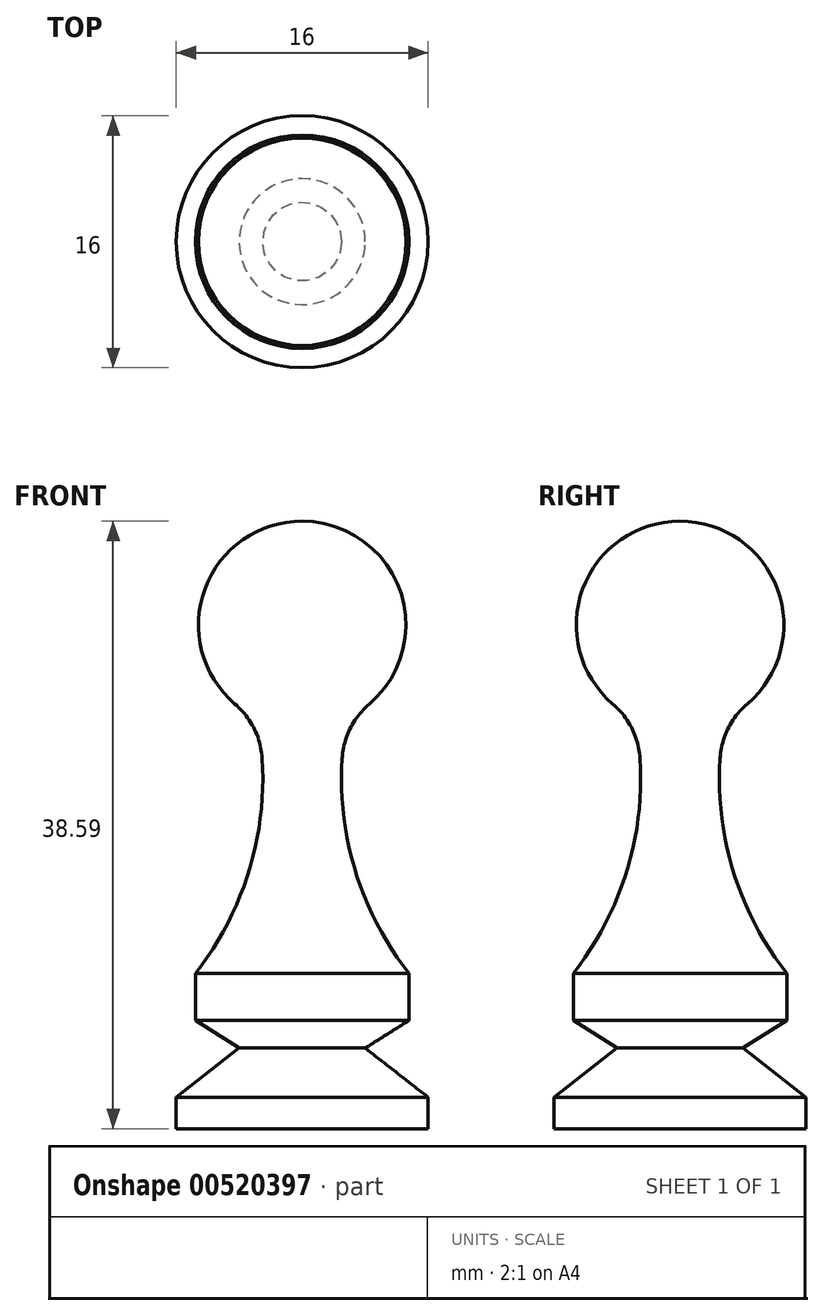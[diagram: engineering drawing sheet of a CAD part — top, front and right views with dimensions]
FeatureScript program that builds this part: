
annotation { "Feature Type Name" : "Feature", "Feature Type Description" : "" }
export const myFeature = defineFeature(function(context is Context, id is Id, definition is map)
    precondition{}
    {
        {
            var Q0;
            Q0=qCreatedBy(makeId("Front.planeOp"),FACE);
            var sketch = newSketch(context, id + "F0", { "sketchPlane" : qUnion([Q0])});
            skArc(sketch, "E0", {"start": v(0, 38.6) * mm, "mid": v(-6.42, 33.47) * mm, "end": v(-2.87, 26.07) * mm});
            skLineSegment(sketch, "E1", {"start": v(0, 0) * mm, "end": v(-8, 0) * mm});
            skLineSegment(sketch, "E2", {"start": v(-8, 0) * mm, "end": v(-8, 2) * mm});
            skLineSegment(sketch, "E3", {"start": v(-8, 2) * mm, "end": v(0, 2) * mm});
            skLineSegment(sketch, "E4", {"start": v(0, 38.6) * mm, "end": v(0, 0) * mm});
            skLineSegment(sketch, "E5", {"start": v(-2.87, 26.07) * mm, "end": v(0, 26.07) * mm});
            skPoint(sketch, "E6.start.orphan", {"position": v(0, 5.14) * mm});
            skLineSegment(sketch, "E7", {"start": v(-4, 5.12) * mm, "end": v(-8, 2) * mm});
            skLineSegment(sketch, "E8", {"start": v(-4, 5.12) * mm, "end": v(0, 5.14) * mm});
            skLineSegment(sketch, "E9", {"start": v(0, 32) * mm, "end": v(0, 0) * mm});
            skLineSegment(sketch, "E10", {"start": v(-6.78, 6.87) * mm, "end": v(0, 6.87) * mm});
            skLineSegment(sketch, "E11", {"start": v(-6.78, 6.87) * mm, "end": v(-6.78, 9.87) * mm});
            skLineSegment(sketch, "E12", {"start": v(-4, 5.12) * mm, "end": v(-6.78, 6.87) * mm});
            skArc(sketch, "E13", {"start": v(-6.78, 9.87) * mm, "mid": v(-3.06, 17.54) * mm, "end": v(-2.87, 26.07) * mm});
            skSolve(sketch);
        }
        {
            var Q0;
            Q0=makeQuery(id+"F0.imprint","IMPRINT",FACE,{"disambiguationData":[TD([[makeQuery(id+"F0.imprint","IMPRINT",EDGE,{"derivedFrom":sQuery(id+"F0.wireOp",EDGE,"E0")}),1.0]])]});
            var Q1;
            {var subQ0=sQuery(id+"F0.wireOp",EDGE,"E1");Q1=makeQuery(id+"F0.imprint","IMPRINT",FACE,{"disambiguationData":[TD([[makeQuery(id+"F0.imprint","IMPRINT",EDGE,{"derivedFrom":subQ0}),-1.0]])]});}
            var Q2;
            {var subQ0=sQuery(id+"F0.wireOp",EDGE,"E3");Q2=makeQuery(id+"F0.imprint","IMPRINT",FACE,{"disambiguationData":[TD([[makeQuery(id+"F0.imprint","IMPRINT",EDGE,{"derivedFrom":subQ0}),1.0]])]});}
            var Q3;
            {var subQ0=sQuery(id+"F0.wireOp",EDGE,"E8");Q3=makeQuery(id+"F0.imprint","IMPRINT",FACE,{"disambiguationData":[TD([[makeQuery(id+"F0.imprint","IMPRINT",EDGE,{"derivedFrom":subQ0}),1.0]])]});}
            var Q4;
            {var subQ2=sQuery(id+"F0.wireOp",EDGE,"E5");Q4=makeQuery(id+"F0.imprint","IMPRINT",FACE,{"disambiguationData":[TD([[makeQuery(id+"F0.imprint","IMPRINT",EDGE,{"derivedFrom":subQ2}),-1.0]])]});}
            var Q5;
            Q5=sQuery(id+"F0.wireOp",EDGE,"E4");
            revolve(context, id + "F1", {"entities" : qUnion([Q0, Q1, Q2, Q3, Q4]), "axis" : qUnion([Q5]), "revolveType" : RevolveType.FULL});
        }
        {
            var Q0;
            Q0=makeQuery(id+"F1.opRevolve","SWEPT_EDGE",EDGE,{"disambiguationData":[OSD([sQuery(id+"F0.wireOp",EDGE,"E0"),sQuery(id+"F0.wireOp",EDGE,"E5"),sQuery(id+"F0.wireOp",EDGE,"E13")])]});
            fillet(context, id + "F2", {"entities" : qUnion([Q0]), "radius" : 5 * mm, "tangentPropagation" : true, "allowEdgeOverflow" : false});
        }
    });
